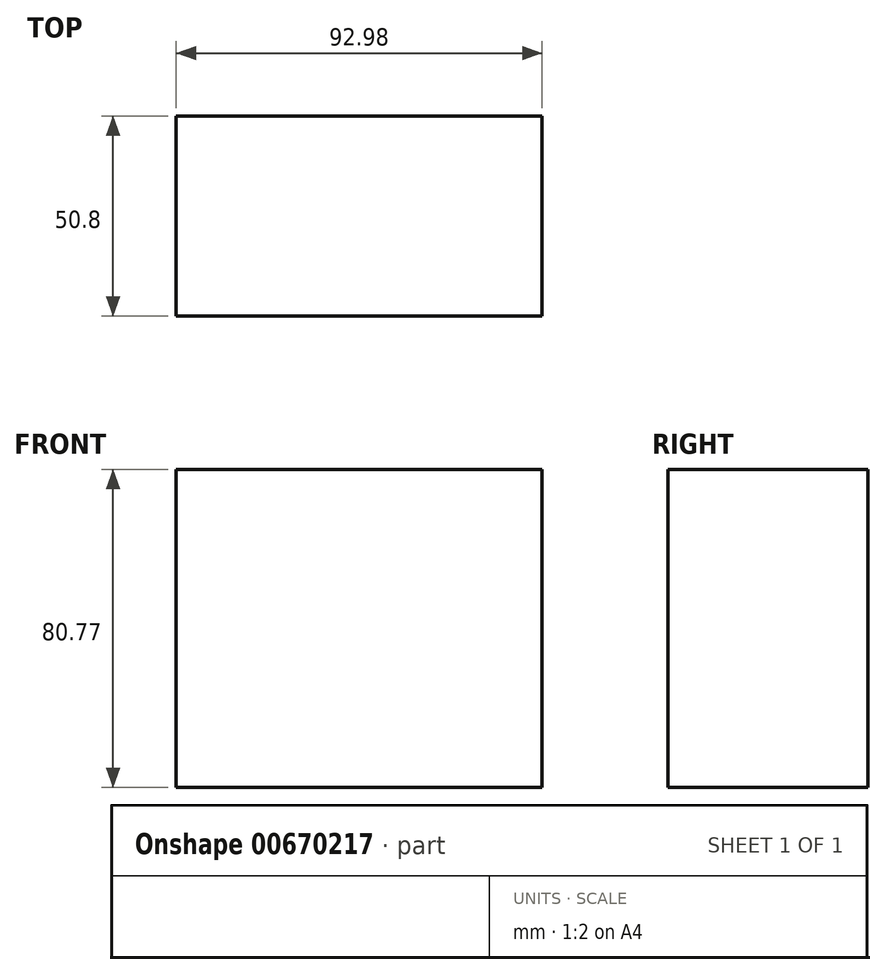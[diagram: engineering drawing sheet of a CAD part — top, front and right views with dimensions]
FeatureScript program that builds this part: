
annotation { "Feature Type Name" : "Feature", "Feature Type Description" : "" }
export const myFeature = defineFeature(function(context is Context, id is Id, definition is map)
    precondition{}
    {
        {
            var Q0;
            Q0=qCreatedBy(makeId("Front.planeOp"),FACE);
            var sketch = newSketch(context, id + "F0", { "sketchPlane" : qUnion([Q0])});
            skLineSegment(sketch, "E0.bottom", {"start": v(59.76, 13.51) * mm, "end": v(-33.22, 13.51) * mm});
            skLineSegment(sketch, "E0.top", {"start": v(59.76, -67.26) * mm, "end": v(-33.22, -67.26) * mm});
            skLineSegment(sketch, "E0.left", {"start": v(59.76, 13.51) * mm, "end": v(59.76, -67.26) * mm});
            skLineSegment(sketch, "E0.right", {"start": v(-33.22, 13.51) * mm, "end": v(-33.22, -67.26) * mm});
            skSolve(sketch);
        }
        {
            var Q0;
            Q0=makeQuery(id+"F0.imprint","IMPRINT",FACE,{"disambiguationData":[TD([[makeQuery(id+"F0.imprint","IMPRINT",EDGE,{"derivedFrom":sQuery(id+"F0.wireOp",EDGE,"E0.bottom")}),1.0]])]});
            extrude(context, id + "F1", {"entities" : qUnion([Q0]), "depth" : 50.8 * mm, "offsetDistance" : 25.4 * mm});
        }
    });
